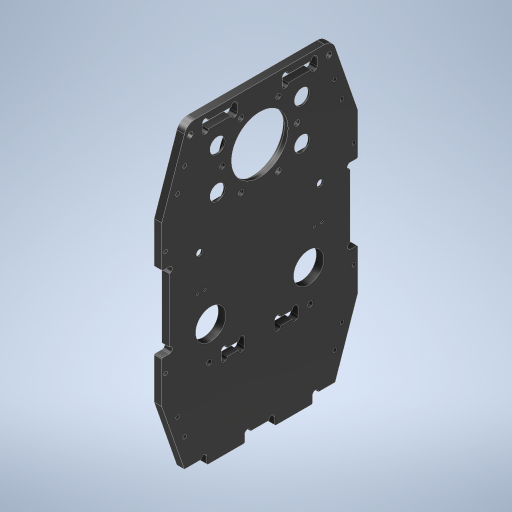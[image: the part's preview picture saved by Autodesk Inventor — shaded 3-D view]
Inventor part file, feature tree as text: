
AUTODESK INVENTOR PART (.ipt)
format: ipt  version: 2024.2 (Build 282272000, 272)  size: 1,179,136 bytes
history: native  units: mm
features: hole x6, sketch x2, extrude x2, mirror x2, chamfer x1
ambient origin geometry x8: Origin, YZ Plane, XZ Plane, XY Plane, X Axis, Y Axis, Z Axis, Center Point
bodies: Solid1 (feature_tree)
feature tree (13):
  sketch  "Sketch1"  dims[d0=37.5mm d1=161.5mm]
  extrude  "Extrusion1"  Depth=161.5mm
  extrude  "Extrusion3"  Depth=1.0mm TaperAngle=360.0deg
  hole  "Ph3.5"  [1 undecoded]
  hole  "Phi3.5-6.1"  [1 undecoded]
  hole  "Phi41-H7"  [1 undecoded]
  chamfer  "C0.5"  Distance=6.0mm
  mirror  "Mirror1"
  hole  "Phi10.0"  [1 undecoded]
  hole  "Phi4.0"  [1 undecoded]
  hole  "Bottom-M3"  [1 undecoded]
  mirror  "Mirror2"
  sketch  "Sketch3"  dims[d2=58.0mm d14=60.0mm d16=360.0deg d18=49.5mm d20=20.0mm d21=5.0mm d23=6.0mm d24=0.025mm d26=5.0mm d27=21.25mm d31=5.0mm d32=50.5mm d34=0.05mm d35=2.0mm d36=0.05mm d37=8.0mm d38=20.0mm d39=20.0mm d40=25.0mm d41=25.0mm d52=0.05mm d53=0.05mm d59=5.0mm d60=0.0mm d63=3.5mm d64=6.0mm d65=6.1mm d66=3.5mm d67=90.0deg d68=8.0mm d69=20.594885mm d70=1.567mm d71=4.0mm d72=4.0mm d73=2.0mm d74=90.0deg d75=8.0mm d76=20.594885mm d77=3.5mm d78=4.0mm d79=4.0mm d80=2.0mm d81=90.0deg d82=8.0mm d83=20.594885mm d98=0.5mm d99=2.0mm d100=45.0deg d105=4.0mm d106=4.0mm d107=0.0mm d108=8.0mm d110=5.0mm d126=3.5mm d136=3.5mm d142=3.0mm d143=41.0mm d144=6.0mm d145=6.1mm d146=3.5mm d147=90.0deg d148=2.5mm d149=0.0mm d156=2.5mm d157=2.5mm d158=15.5mm d160=50.0mm d162=5.0mm d167=20.0mm d169=65.0mm d171=20.0mm d180=1.0mm d181=22.5mm d182=5.0mm d183=10.0mm d184=197.5mm d186=30.0mm d187=100.0mm d188=12.0mm d189=3.320595mm d198=20.0mm d201=5.0mm d202=15.0mm d205=55.0mm d212=2.459mm d213=6.0mm d214=12.5mm d215=1.0mm d216=90.0deg d217=8.0mm d218=20.594885mm d219=12.5mm d220=2.0mm d221=2.0mm d222=2.0mm d223=210.0mm d224=7.5mm d225=27.0mm d226=27.0mm d229=25.0mm d230=9.0mm d233=4.0mm d235=2.0mm d236=10.0mm d237=6.0mm d238=12.5mm d239=10.0mm d240=90.0deg d241=8.0mm d242=20.594885mm d243=4.0mm d244=4.0mm d246=1.0mm d248=70.0mm d249=2.0mm d250=105.5mm d252=1.5mm d253=130.0mm d254=2.0mm d255=1.5mm d259=2.0mm d261=4.0mm d262=20.0mm d263=6.5mm d264=5.0mm d270=3.0mm d274=4.5mm d276=4.0mm d277=6.0mm d278=4.0mm d279=2.0mm d280=90.0deg d281=8.0mm d282=20.594885mm d283=2.459mm d284=6.0mm d285=4.0mm d286=2.0mm d287=90.0deg d288=6.0mm d289=0.0mm d251=1.0mm d256=0.75mm d257=20.594885mm d258=0.0625mm d260=0.375mm]
note: 6 required parameter values undecoded (feature->parameter linkage not recoverable at this tier; creation-order binding heuristic only, values carry confidence <= 0.55)
